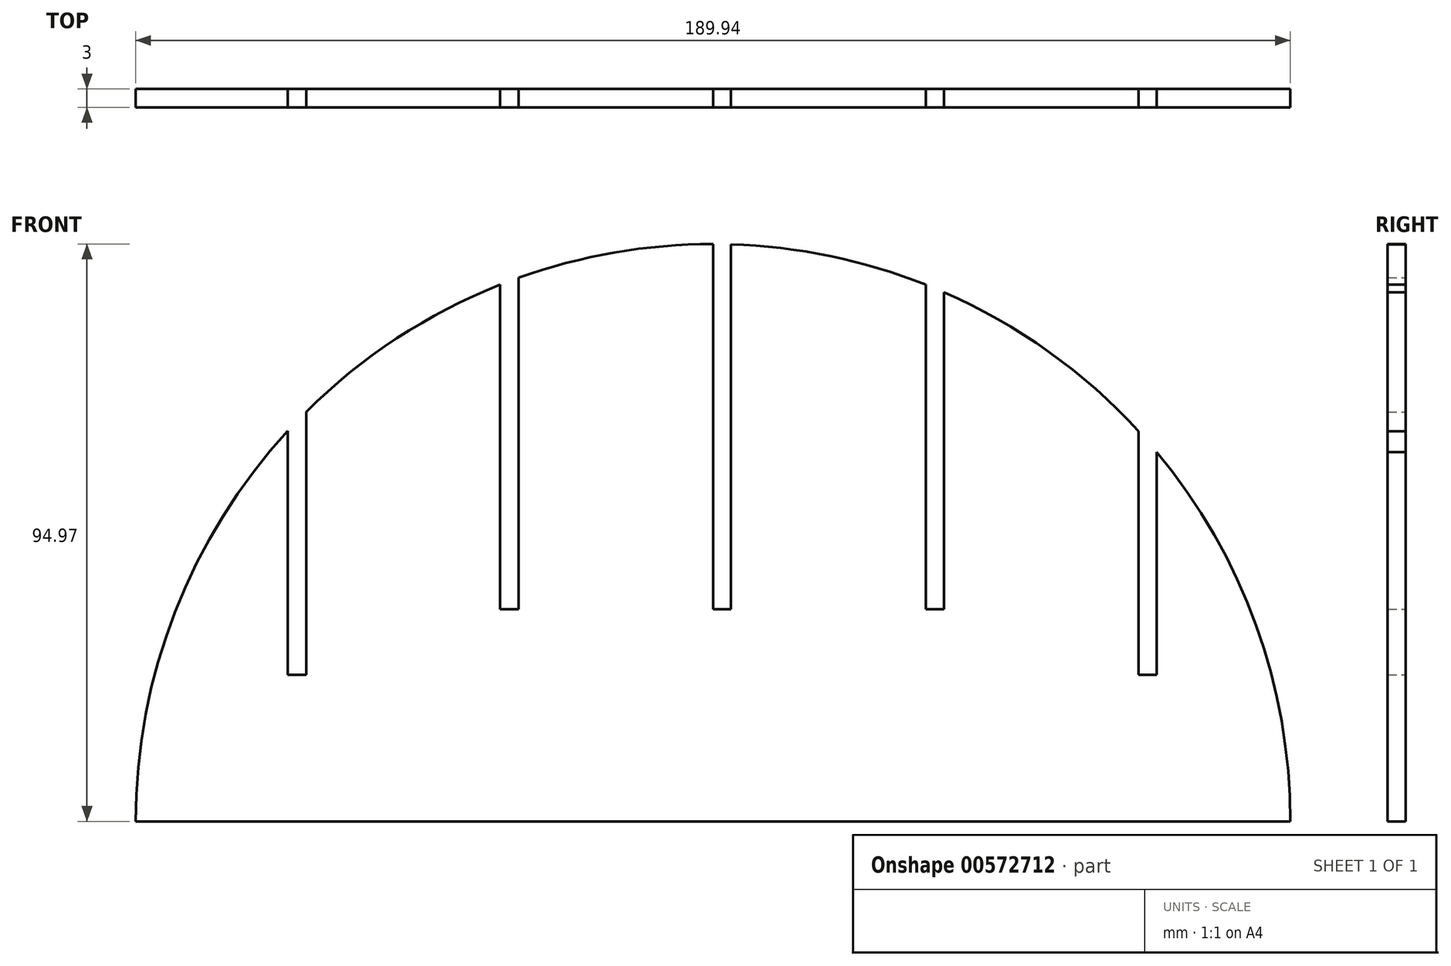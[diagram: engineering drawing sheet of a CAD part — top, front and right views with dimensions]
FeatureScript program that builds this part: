
annotation { "Feature Type Name" : "Feature", "Feature Type Description" : "" }
export const myFeature = defineFeature(function(context is Context, id is Id, definition is map)
    precondition{}
    {
        {
            var Q0;
            Q0=qCreatedBy(makeId("Front.planeOp"),FACE);
            var sketch = newSketch(context, id + "F0", { "sketchPlane" : qUnion([Q0])});
            skLineSegment(sketch, "E0", {"start": v(94.97, 0) * mm, "end": v(-95.03, 0) * mm});
            skArc(sketch, "E1", {"start": v(94.97, 0) * mm, "mid": v(89.3, 32.3) * mm, "end": v(73, 60.75) * mm});
            skLineSegment(sketch, "E2", {"start": v(-94.97, 0) * mm, "end": v(-69.93, 0) * mm});
            skLineSegment(sketch, "E3", {"start": v(94.97, 0) * mm, "end": v(70, 0) * mm});
            skLineSegment(sketch, "E4", {"start": v(-69.93, 24.1) * mm, "end": v(-69.93, 64.26) * mm});
            skLineSegment(sketch, "E5", {"start": v(-69.93, 0) * mm, "end": v(-35, 0) * mm});
            skLineSegment(sketch, "E6", {"start": v(-35, 0) * mm, "end": v(0, 0) * mm});
            skLineSegment(sketch, "E7", {"start": v(0, 0) * mm, "end": v(35, 0) * mm});
            skLineSegment(sketch, "E8", {"start": v(35, 0) * mm, "end": v(70, 0) * mm});
            skLineSegment(sketch, "E9", {"start": v(-69.93, 64.26) * mm, "end": v(-69.93, 24.1) * mm});
            skLineSegment(sketch, "E10", {"start": v(-35, 34.92) * mm, "end": v(-35, 88.28) * mm});
            skLineSegment(sketch, "E11", {"start": v(0, 34.92) * mm, "end": v(0, 94.97) * mm});
            skLineSegment(sketch, "E12", {"start": v(35, 34.92) * mm, "end": v(35, 88.28) * mm});
            skLineSegment(sketch, "E13", {"start": v(70, 24.1) * mm, "end": v(70, 64.18) * mm});
            skLineSegment(sketch, "E14", {"start": v(-35, 88.28) * mm, "end": v(-35, 34.92) * mm});
            skLineSegment(sketch, "E15", {"start": v(0, 34.92) * mm, "end": v(2.96, 34.92) * mm});
            skPoint(sketch, "E16", {"position": v(0, 34.92) * mm});
            skPoint(sketch, "E17", {"position": v(35, 34.92) * mm});
            skLineSegment(sketch, "E18", {"start": v(-69.93, 24.1) * mm, "end": v(-66.93, 24.1) * mm});
            skPoint(sketch, "E19", {"position": v(-66.93, 24.1) * mm});
            skPoint(sketch, "E20", {"position": v(-32, 34.92) * mm});
            skPoint(sketch, "E21", {"position": v(2.96, 34.92) * mm});
            skPoint(sketch, "E22", {"position": v(38, 34.92) * mm});
            skPoint(sketch, "E23", {"position": v(73, 24.1) * mm});
            skLineSegment(sketch, "E24", {"start": v(-66.93, 24.1) * mm, "end": v(-66.93, 67.38) * mm});
            skArc(sketch, "E25.trimOffspring", {"start": v(-69.93, 64.26) * mm, "mid": v(-88.49, 34.48) * mm, "end": v(-94.97, 0) * mm});
            skPoint(sketch, "E26.orphan", {"position": v(70, 24.1) * mm});
            skLineSegment(sketch, "E27", {"start": v(-32, 34.92) * mm, "end": v(-32, 89.42) * mm});
            skLineSegment(sketch, "E28", {"start": v(70, 24.1) * mm, "end": v(73, 24.1) * mm});
            skLineSegment(sketch, "E29", {"start": v(-35, 34.92) * mm, "end": v(-32, 34.92) * mm});
            skLineSegment(sketch, "E30", {"start": v(35, 34.92) * mm, "end": v(38, 34.92) * mm});
            skArc(sketch, "E31.trimOffspring", {"start": v(-35, 88.28) * mm, "mid": v(-52.03, 79.45) * mm, "end": v(-66.93, 67.38) * mm});
            skLineSegment(sketch, "E32", {"start": v(2.96, 34.92) * mm, "end": v(2.96, 94.92) * mm});
            skLineSegment(sketch, "E33", {"start": v(38, 34.92) * mm, "end": v(38, 87.04) * mm});
            skArc(sketch, "E34.trimOffspring", {"start": v(0, 94.97) * mm, "mid": v(-16.24, 93.57) * mm, "end": v(-32, 89.42) * mm});
            skArc(sketch, "E35.trimOffspring", {"start": v(35, 88.28) * mm, "mid": v(19.27, 93) * mm, "end": v(2.96, 94.92) * mm});
            skLineSegment(sketch, "E36", {"start": v(73, 24.1) * mm, "end": v(73, 60.75) * mm});
            skArc(sketch, "E37.trimOffspring", {"start": v(70, 64.18) * mm, "mid": v(55.2, 77.28) * mm, "end": v(38, 87.04) * mm});
            skSolve(sketch);
        }
        {
            var Q0;
            Q0=qSketchRegion(id+"F0",true);
            extrude(context, id + "F1", {"entities" : qUnion([Q0]), "depth" : 3 * mm, "offsetDistance" : 25 * mm});
        }
    });
